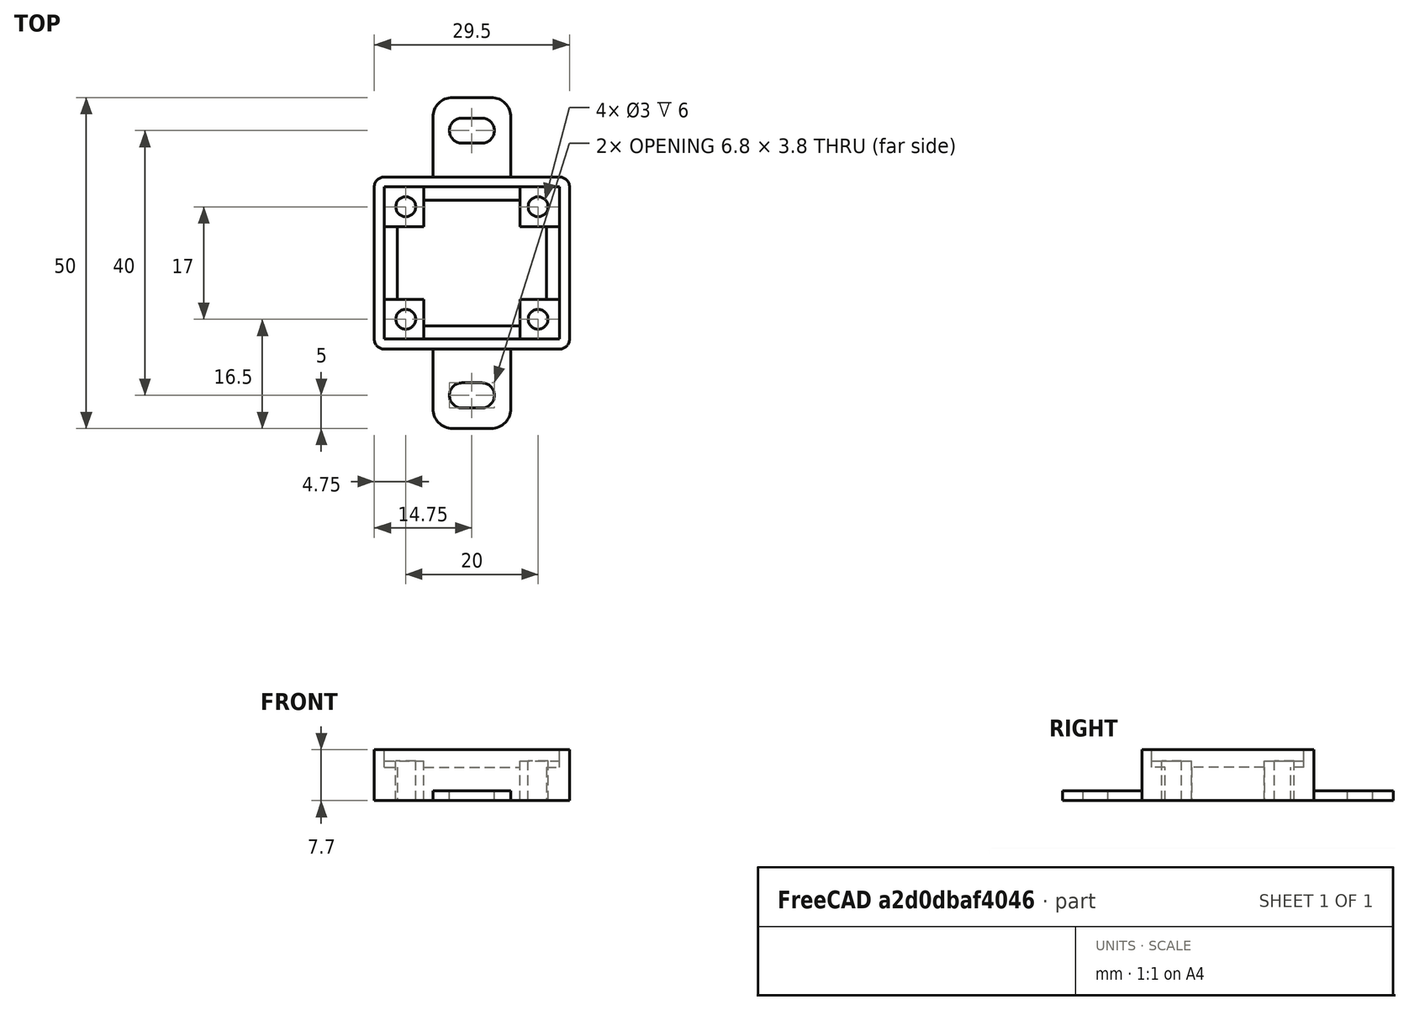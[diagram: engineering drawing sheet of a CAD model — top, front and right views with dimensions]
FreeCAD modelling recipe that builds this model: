
FCSTD DOCUMENT  (FreeCAD 0.19R23578 (Git))
Label: ina219_dc_current_sensor
License: All rights reserved
LicenseURL: http://en.wikipedia.org/wiki/All_rights_reserved
objects: Part::Box×4, Part::MultiFuse×3, Part::FeaturePython×2, Part::Cut×2, Spreadsheet::Sheet×1, Part::Cylinder×1, Part::Fillet×1, Part::Feature×1, App::Part×1
note: 14 computed .brp shape members not serialized (recipe doc carries the construction recipe); baked Part::Feature solids carry a one-line shape summary decoded from their .brp

FEATURE [Spreadsheet::Sheet] Spreadsheet  label="p"
  cells = A1=hole_x_dist; B1(hole_x_dist)=20; A2=hole_y_dist; B2(hole_y_dist)=17; A3=pcb_under; B3(pcb_under)=3; A4=pcb_x; B4(pcb_x)=26.5; A5=pcb_y; B5(pcb_y)=23; A6=hole_stand_x; B6(hole_stand_x)=6; A7=hole_stand_y; B7(hole_stand_y)=6; A8=hole_r; B8(hole_r)=1.5; A9=box_wall; B9(box_wall)=1.5; A10=under_layer; B10(under_layer)=3; A11=pcb_height; B11(pcb_height)=1.7; A12=under_pcb_border; B12(under_pcb_border)=2
FEATURE [Part::Box] Box  label="bottom cube"
  AttacherType = Attacher::AttachEngine3D
  Height = 7.7
  Length = 29.5
  Width = 26
  expr: Width = <<p>>.pcb_y + <<p>>.box_wall * 2
  expr: Length = <<p>>.pcb_x + <<p>>.box_wall * 2
  expr: Height = <<p>>.pcb_under + <<p>>.pcb_height + <<p>>.under_layer
FEATURE [Part::Box] Box001  label="bottom extraction"
  AttacherType = Attacher::AttachEngine3D
  Height = 10
  Length = 22.5
  Placement = pos=(3.5,3.5,0) rot=(0,0,1;0rad)
  Width = 19
  expr: .Placement.Base.y = <<p>>.under_pcb_border + <<p>>.box_wall
  expr: .Placement.Base.x = <<p>>.under_pcb_border + <<p>>.box_wall
  expr: Length = <<p>>.pcb_x - <<p>>.under_pcb_border * 2
  expr: Width = <<p>>.pcb_y - <<p>>.under_pcb_border * 2
FEATURE [Part::Box] Box002  label="pcb extraction"
  AttacherType = Attacher::AttachEngine3D
  Height = 10
  Length = 26.5
  Placement = pos=(1.5,1.5,5) rot=(0,0,1;0rad)
  Width = 23
  expr: .Placement.Base.z = <<p>>.under_pcb_border + <<p>>.under_layer
  expr: .Placement.Base.y = <<p>>.box_wall
  expr: .Placement.Base.x = <<p>>.box_wall
  expr: Length = <<p>>.pcb_x
  expr: Width = <<p>>.pcb_y
FEATURE [Part::MultiFuse] Fusion  label="bottom extraction001"
  Shapes = -> [Box001,Box002]
FEATURE [Part::Box] Box003  label="hole stand cube"
  AttacherType = Attacher::AttachEngine3D
  Height = 6
  Length = 6
  Placement = pos=(1.5,1.5,0) rot=(0,0,1;0rad)
  Width = 6
  expr: .Placement.Base.y = <<p>>.box_wall
  expr: .Placement.Base.x = <<p>>.box_wall
  expr: Height = <<p>>.pcb_under + <<p>>.under_layer
  expr: Width = <<p>>.hole_stand_y
  expr: Length = <<p>>.hole_stand_x
FEATURE [Part::FeaturePython] Array  label="hole stand array"  # Draft array (typed FeaturePython)
  Angle = 360
  ArrayType = 0
  Axis = (0,0,1)
  Base = -> Box003
  Center = (0,0,0)
  Fuse = false
  IntervalAxis = (0,0,0)
  IntervalX = (20.5,0,0)
  IntervalY = (0,17,0)
  IntervalZ = (0,0,1)
  NumberPolar = 1
  NumberX = 2
  NumberY = 2
  NumberZ = 1
  expr: .IntervalY.y = <<p>>.pcb_y - <<p>>.hole_stand_y
  expr: .IntervalX.x = <<p>>.pcb_x - <<p>>.hole_stand_x
FEATURE [Part::Cylinder] Cylinder  label="pcb hole"
  Angle = 360
  AttacherType = Attacher::AttachEngine3D
  Height = 10
  Placement = pos=(4.75,4.5,0) rot=(0,0,1;0rad)
  Radius = 1.5
  expr: .Placement.Base.y = (<<p>>.box_wall * 2 + <<p>>.pcb_y - <<p>>.hole_y_dist) / 2
  expr: .Placement.Base.x = (<<p>>.box_wall * 2 + <<p>>.pcb_x - <<p>>.hole_x_dist) / 2
  expr: Radius = <<p>>.hole_r
FEATURE [Part::FeaturePython] Array001  label="hole array"  # Draft array (typed FeaturePython)
  Angle = 360
  ArrayType = 0
  Axis = (0,0,1)
  Base = -> Cylinder
  Center = (0,0,0)
  Fuse = false
  IntervalAxis = (0,0,0)
  IntervalX = (20,0,0)
  IntervalY = (0,17,0)
  IntervalZ = (0,0,1)
  NumberPolar = 1
  NumberX = 2
  NumberY = 2
  NumberZ = 1
  expr: .IntervalY.y = <<p>>.hole_y_dist
  expr: .IntervalX.x = <<p>>.hole_x_dist
FEATURE [Part::Fillet] Fillet001  label="bottom cube fillet"
  Base = -> Box
  Edges = 4 edges r=1.5: [Edge1,Edge3,Edge5,Edge7]
FEATURE [Part::Feature] Cut002001  label="attach plane y dir001"
  Placement = pos=(8.85,-12,0) rot=(0,0,1;0rad)
  shape: bbox 11.8 x 50 x 1.5 mm, 20 faces (baked)
FEATURE [Part::MultiFuse] Fusion002  label="bottom fusion"
  Shapes = -> [Fillet001,Cut002001]
FEATURE [Part::Cut] Cut  label="pcb box cut"
  Base = -> Fusion002
  Tool = -> Fusion
FEATURE [Part::MultiFuse] Fusion001  label="frame fusion"
  Shapes = -> [Array,Cut]
FEATURE [Part::Cut] Cut001  label="frame fusion with holes"
  Base = -> Fusion001
  Tool = -> Array001
FEATURE [App::Part] Part  label="pcb with 4 holes part"
  Group = -> [Fusion,Fusion002,Box002,Box003,Box001,Array001,Cut,Array,Cylinder,Fusion001,Cut001]
  Origin = -> Origin
